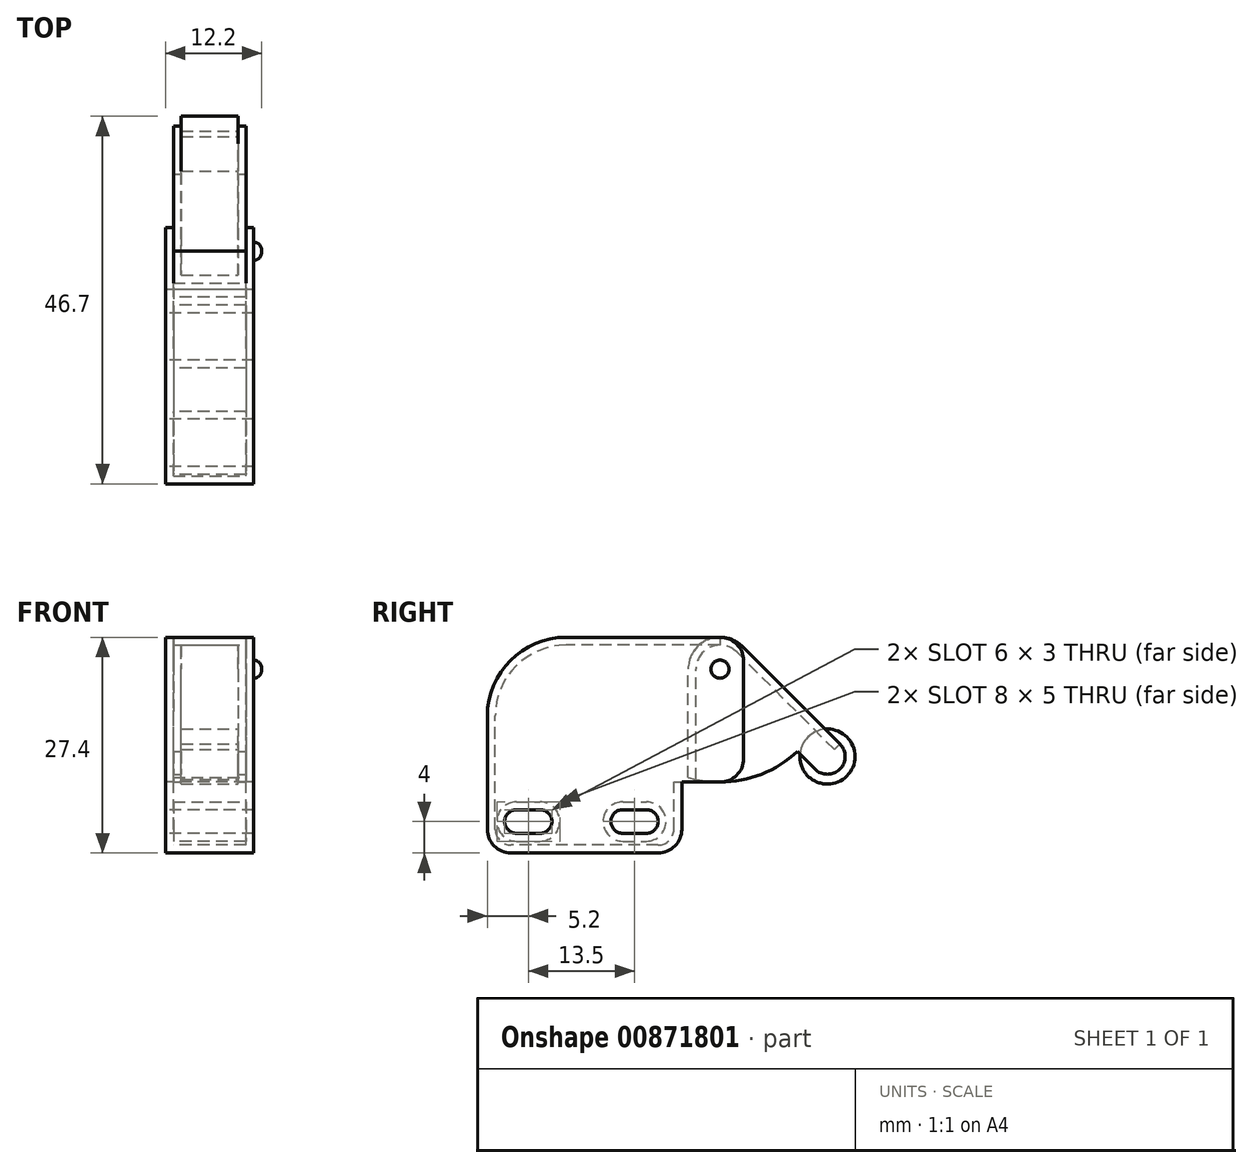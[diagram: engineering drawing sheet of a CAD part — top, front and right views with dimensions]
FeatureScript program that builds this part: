
annotation { "Feature Type Name" : "Feature", "Feature Type Description" : "" }
export const myFeature = defineFeature(function(context is Context, id is Id, definition is map)
    precondition{}
    {
        {
            var Q0;
            Q0=qCreatedBy(makeId("Right.planeOp"),FACE);
            var sketch = newSketch(context, id + "F0", { "sketchPlane" : qUnion([Q0])});
            skLineSegment(sketch, "E0.bottom", {"start": v(12.35, -13.7) * mm, "end": v(-12.35, -13.7) * mm});
            skLineSegment(sketch, "E0.top", {"start": v(12.35, 13.7) * mm, "end": v(-12.35, 13.7) * mm});
            skLineSegment(sketch, "E0.left", {"start": v(12.35, -13.7) * mm, "end": v(12.35, -4.7) * mm});
            skLineSegment(sketch, "E0.right", {"start": v(-12.35, -13.7) * mm, "end": v(-12.35, 13.7) * mm});
            skPoint(sketch, "E0.middle", {"position": v(0, 0) * mm});
            skLineSegment(sketch, "E1", {"start": v(-8.65, -9.7) * mm, "end": v(-5.65, -9.7) * mm});
            skLineSegment(sketch, "E2", {"start": v(4.85, -9.7) * mm, "end": v(7.85, -9.7) * mm});
            skPoint(sketch, "E3", {"position": v(-7.15, -9.7) * mm});
            skPoint(sketch, "E4", {"position": v(6.35, -9.7) * mm});
            skArc(sketch, "E5.0.startCap", {"start": v(-8.65, -11.2) * mm, "mid": v(-10.15, -9.7) * mm, "end": v(-8.65, -8.2) * mm});
            skArc(sketch, "E5.0.endCap", {"start": v(-5.65, -8.2) * mm, "mid": v(-4.15, -9.7) * mm, "end": v(-5.65, -11.2) * mm});
            skLineSegment(sketch, "E5.0.left", {"start": v(-8.65, -8.2) * mm, "end": v(-5.65, -8.2) * mm});
            skLineSegment(sketch, "E5.0.right", {"start": v(-8.65, -11.2) * mm, "end": v(-5.65, -11.2) * mm});
            skArc(sketch, "E5.1.startCap", {"start": v(7.85, -8.2) * mm, "mid": v(9.35, -9.7) * mm, "end": v(7.85, -11.2) * mm});
            skArc(sketch, "E5.1.endCap", {"start": v(4.85, -11.2) * mm, "mid": v(3.35, -9.7) * mm, "end": v(4.85, -8.2) * mm});
            skLineSegment(sketch, "E5.1.left", {"start": v(4.85, -11.2) * mm, "end": v(7.85, -11.2) * mm});
            skLineSegment(sketch, "E5.1.right", {"start": v(4.85, -8.2) * mm, "end": v(7.85, -8.2) * mm});
            skLineSegment(sketch, "E6", {"start": v(12.35, -4.7) * mm, "end": v(20.2, -4.7) * mm});
            skLineSegment(sketch, "E7", {"start": v(20.2, -4.7) * mm, "end": v(20.2, 13.7) * mm});
            skLineSegment(sketch, "E8", {"start": v(20.2, 13.7) * mm, "end": v(12.35, 13.7) * mm});
            skSolve(sketch);
        }
        {
            var Q0;
            Q0=makeQuery(id+"F0.imprint","IMPRINT",FACE,{"disambiguationData":[TD([[makeQuery(id+"F0.imprint","IMPRINT",EDGE,{"derivedFrom":sQuery(id+"F0.wireOp",EDGE,"E0.bottom")}),-1.0]])]});
            extrude(context, id + "F1", {"entities" : qUnion([Q0]), "depth" : 11.2 * mm, "offsetDistance" : 25 * mm});
        }
        {
            var Q0;
            Q0=makeQuery(id+"F1.opExtrude","SWEPT_EDGE",EDGE,{"disambiguationData":[OSD([sQuery(id+"F0.wireOp",EDGE,"E0.bottom"),sQuery(id+"F0.wireOp",EDGE,"E0.right")])]});
            var Q1;
            Q1=makeQuery(id+"F1.opExtrude","SWEPT_EDGE",EDGE,{"disambiguationData":[OSD([sQuery(id+"F0.wireOp",EDGE,"E0.bottom"),sQuery(id+"F0.wireOp",EDGE,"E0.left")])]});
            var Q2;
            Q2=makeQuery(id+"F1.opExtrude","SWEPT_EDGE",EDGE,{"disambiguationData":[OSD([sQuery(id+"F0.wireOp",EDGE,"E6"),sQuery(id+"F0.wireOp",EDGE,"E7")])]});
            var Q3;
            Q3=makeQuery(id+"F1.opExtrude","SWEPT_EDGE",EDGE,{"disambiguationData":[OSD([sQuery(id+"F0.wireOp",EDGE,"E7"),sQuery(id+"F0.wireOp",EDGE,"E8")])]});
            fillet(context, id + "F2", {"entities" : qUnion([Q0, Q1, Q2, Q3]), "tangentPropagation" : true, "radius" : 3 * mm, "defaultsChanged" : false, "vertexSettings" : [], "allowEdgeOverflow" : false});
        }
        {
            var Q0;
            Q0=makeQuery(id+"F1.opExtrude","SWEPT_EDGE",EDGE,{"disambiguationData":[OSD([sQuery(id+"F0.wireOp",EDGE,"E0.top"),sQuery(id+"F0.wireOp",EDGE,"E0.right")])]});
            fillet(context, id + "F3", {"entities" : qUnion([Q0]), "tangentPropagation" : true, "radius" : 10 * mm, "defaultsChanged" : true, "vertexSettings" : [], "allowEdgeOverflow" : false});
        }
        {
            var Q0;
            Q0=makeQuery(id+"F1.opExtrude","SWEPT_FACE",FACE,{"disambiguationData":[OSD([sQuery(id+"F0.wireOp",EDGE,"E6")])]});
            var Q1;
            Q1=makeQuery(id+"F2.opFillet","BLEND_FACE",FACE,{"disambiguationData":[OSD([sQuery(id+"F0.wireOp",EDGE,"E6"),sQuery(id+"F0.wireOp",EDGE,"E7")])]});
            var Q2;
            Q2=makeQuery(id+"F1.opExtrude","SWEPT_FACE",FACE,{"disambiguationData":[OSD([sQuery(id+"F0.wireOp",EDGE,"E7")])]});
            var Q3;
            Q3=makeQuery(id+"F2.opFillet","BLEND_FACE",FACE,{"disambiguationData":[OSD([sQuery(id+"F0.wireOp",EDGE,"E7"),sQuery(id+"F0.wireOp",EDGE,"E8")])]});
            shell(context, id + "F4", {"entities" : qUnion([Q0, Q1, Q2, Q3]), "thickness" : 1 * mm});
        }
        {
            var Q0;
            Q0=makeQuery(id+"F1.opExtrude","CAP_FACE",FACE,{"disambiguationData":[OSD([sQuery(id+"F0.wireOp",EDGE,"E0.bottom"),sQuery(id+"F0.wireOp",EDGE,"E0.top"),sQuery(id+"F0.wireOp",EDGE,"E0.left"),sQuery(id+"F0.wireOp",EDGE,"E0.right"),sQuery(id+"F0.wireOp",EDGE,"E5.0.startCap"),sQuery(id+"F0.wireOp",EDGE,"E5.0.endCap"),sQuery(id+"F0.wireOp",EDGE,"E5.0.left"),sQuery(id+"F0.wireOp",EDGE,"E5.0.right"),sQuery(id+"F0.wireOp",EDGE,"E5.1.startCap"),sQuery(id+"F0.wireOp",EDGE,"E5.1.endCap"),sQuery(id+"F0.wireOp",EDGE,"E5.1.left"),sQuery(id+"F0.wireOp",EDGE,"E5.1.right"),sQuery(id+"F0.wireOp",EDGE,"E6"),sQuery(id+"F0.wireOp",EDGE,"E7"),sQuery(id+"F0.wireOp",EDGE,"E8")])],"isStart":false});
            var sketch = newSketch(context, id + "F5", { "sketchPlane" : qUnion([Q0])});
            skCircle(sketch, "E9", {"center": v(17.2, 9.65) * mm, "radius": 1.15 * mm});
            skSolve(sketch);
        }
        {
            var Q0;
            Q0=makeQuery(id+"F5.imprint","IMPRINT",FACE,{"disambiguationData":[TD([[makeQuery(id+"F5.imprint","IMPRINT",EDGE,{"derivedFrom":sQuery(id+"F5.wireOp",EDGE,"E9")}),1.0]])]});
            extrude(context, id + "F6", {"entities" : qUnion([Q0]), "operationType" : NewBodyOperationType.ADD, "depth" : 1 * mm, "offsetDistance" : 25 * mm});
        }
        {
            var Q0;
            {var subQ0=sQuery(id+"F0.wireOp",EDGE,"E8");var subQ1=sQuery(id+"F0.wireOp",EDGE,"E7");var subQ2=sQuery(id+"F0.wireOp",EDGE,"E6");var subQ3=sQuery(id+"F0.wireOp",EDGE,"E5.1.right");var subQ4=sQuery(id+"F0.wireOp",EDGE,"E5.1.left");var subQ5=sQuery(id+"F0.wireOp",EDGE,"E5.1.endCap");var subQ6=sQuery(id+"F0.wireOp",EDGE,"E5.1.startCap");var subQ7=sQuery(id+"F0.wireOp",EDGE,"E5.0.right");var subQ8=sQuery(id+"F0.wireOp",EDGE,"E5.0.left");var subQ9=sQuery(id+"F0.wireOp",EDGE,"E5.0.endCap");var subQ10=sQuery(id+"F0.wireOp",EDGE,"E5.0.startCap");var subQ11=sQuery(id+"F0.wireOp",EDGE,"E0.right");var subQ12=sQuery(id+"F0.wireOp",EDGE,"E0.left");var subQ13=sQuery(id+"F0.wireOp",EDGE,"E0.top");var subQ14=sQuery(id+"F0.wireOp",EDGE,"E0.bottom");Q0=makeQuery(id+"F4.opShell","OFFSET_FACE",FACE,{"disambiguationData":[OSD([subQ14,subQ13,subQ12,subQ11,subQ10,subQ9,subQ8,subQ7,subQ6,subQ5,subQ4,subQ3,subQ2,subQ1,subQ0]),TDD([makeQuery(id+"F1.opExtrude","CAP_FACE",FACE,{"disambiguationData":[OSD([subQ14,subQ13,subQ12,subQ11,subQ10,subQ9,subQ8,subQ7,subQ6,subQ5,subQ4,subQ3,subQ2,subQ1,subQ0])],"isStart":false})])]});}
            var sketch = newSketch(context, id + "F7", { "sketchPlane" : qUnion([Q0])});
            skArc(sketch, "E10", {"start": v(-13.15, 9.65) * mm, "mid": v(-15.65, 13.4) * mm, "end": v(-20.06, 12.51) * mm});
            skLineSegment(sketch, "E11", {"start": v(-20.06, 12.51) * mm, "end": v(-32.44, 0.14) * mm});
            skArc(sketch, "E12", {"start": v(-32.44, 0.14) * mm, "mid": v(-32.44, -3.04) * mm, "end": v(-29.26, -3.04) * mm});
            skLineSegment(sketch, "E13", {"start": v(-29.26, -3.04) * mm, "end": v(-27.02, -0.81) * mm});
            skArc(sketch, "E14", {"start": v(-27.02, -0.81) * mm, "mid": v(-20.53, -4.3) * mm, "end": v(-13.15, -4.12) * mm});
            skLineSegment(sketch, "E15", {"start": v(-13.15, 9.65) * mm, "end": v(-13.15, -4.12) * mm});
            skSolve(sketch);
        }
        {
            var Q0;
            Q0 = qSketchRegion(id + "F7", true);
            var Q1;
            {var subQ0=sQuery(id+"F0.wireOp",EDGE,"E8");var subQ1=sQuery(id+"F0.wireOp",EDGE,"E7");var subQ2=sQuery(id+"F0.wireOp",EDGE,"E6");var subQ3=sQuery(id+"F0.wireOp",EDGE,"E5.1.right");var subQ4=sQuery(id+"F0.wireOp",EDGE,"E5.1.left");var subQ5=sQuery(id+"F0.wireOp",EDGE,"E5.1.endCap");var subQ6=sQuery(id+"F0.wireOp",EDGE,"E5.1.startCap");var subQ7=sQuery(id+"F0.wireOp",EDGE,"E5.0.right");var subQ8=sQuery(id+"F0.wireOp",EDGE,"E5.0.left");var subQ9=sQuery(id+"F0.wireOp",EDGE,"E5.0.endCap");var subQ10=sQuery(id+"F0.wireOp",EDGE,"E5.0.startCap");var subQ11=sQuery(id+"F0.wireOp",EDGE,"E0.right");var subQ12=sQuery(id+"F0.wireOp",EDGE,"E0.left");var subQ13=sQuery(id+"F0.wireOp",EDGE,"E0.top");var subQ14=sQuery(id+"F0.wireOp",EDGE,"E0.bottom");Q1=makeQuery(id+"F4.opShell","OFFSET_FACE",FACE,{"disambiguationData":[OSD([subQ14,subQ13,subQ12,subQ11,subQ10,subQ9,subQ8,subQ7,subQ6,subQ5,subQ4,subQ3,subQ2,subQ1,subQ0]),TDD([makeQuery(id+"F1.opExtrude","CAP_FACE",FACE,{"disambiguationData":[OSD([subQ14,subQ13,subQ12,subQ11,subQ10,subQ9,subQ8,subQ7,subQ6,subQ5,subQ4,subQ3,subQ2,subQ1,subQ0])],"isStart":true})])]});}
            extrude(context, id + "F8", {"entities" : qUnion([Q0]), "endBound" : BoundingType.UP_TO_SURFACE, "depth" : 25 * mm, "endBoundEntityFace" : qUnion([Q1]), "offsetDistance" : 25 * mm});
        }
        {
            var Q0;
            Q0=makeQuery(id+"F8.opExtrude","SWEPT_FACE",FACE,{"disambiguationData":[OSD([sQuery(id+"F7.wireOp",EDGE,"E14")])]});
            var Q1;
            Q1=makeQuery(id+"F8.opExtrude","SWEPT_FACE",FACE,{"disambiguationData":[OSD([sQuery(id+"F7.wireOp",EDGE,"E13")])]});
            var Q2;
            Q2=makeQuery(id+"F8.opExtrude","SWEPT_FACE",FACE,{"disambiguationData":[OSD([sQuery(id+"F7.wireOp",EDGE,"E12")])]});
            shell(context, id + "F9", {"entities" : qUnion([Q0, Q1, Q2]), "thickness" : 1 * mm});
        }
        {
            var Q0;
            {var subQ0=sQuery(id+"F7.wireOp",EDGE,"E15");var subQ1=sQuery(id+"F7.wireOp",EDGE,"E14");var subQ2=sQuery(id+"F7.wireOp",EDGE,"E13");var subQ3=sQuery(id+"F7.wireOp",EDGE,"E12");var subQ4=sQuery(id+"F7.wireOp",EDGE,"E11");var subQ5=sQuery(id+"F7.wireOp",EDGE,"E10");Q0=makeQuery(id+"F9.opShell","OFFSET_FACE",FACE,{"disambiguationData":[OSD([subQ5,subQ4,subQ3,subQ2,subQ1,subQ0]),TDD([makeQuery(id+"F8.opExtrude","CAP_FACE",FACE,{"disambiguationData":[OSD([subQ5,subQ4,subQ3,subQ2,subQ1,subQ0])],"isStart":true})])]});}
            var sketch = newSketch(context, id + "F10", { "sketchPlane" : qUnion([Q0])});
            skCircle(sketch, "E16", {"center": v(-30.85, -1.45) * mm, "radius": 3.5 * mm});
            skSolve(sketch);
        }
        {
            var Q0;
            Q0 = qSketchRegion(id + "F10", true);
            var Q1;
            {var subQ0=sQuery(id+"F7.wireOp",EDGE,"E15");var subQ1=sQuery(id+"F7.wireOp",EDGE,"E14");var subQ2=sQuery(id+"F7.wireOp",EDGE,"E13");var subQ3=sQuery(id+"F7.wireOp",EDGE,"E12");var subQ4=sQuery(id+"F7.wireOp",EDGE,"E11");var subQ5=sQuery(id+"F7.wireOp",EDGE,"E10");Q1=makeQuery(id+"F9.opShell","OFFSET_FACE",FACE,{"disambiguationData":[OSD([subQ5,subQ4,subQ3,subQ2,subQ1,subQ0]),TDD([makeQuery(id+"F8.opExtrude","CAP_FACE",FACE,{"disambiguationData":[OSD([subQ5,subQ4,subQ3,subQ2,subQ1,subQ0])],"isStart":false})])]});}
            extrude(context, id + "F11", {"entities" : qUnion([Q0]), "endBound" : BoundingType.UP_TO_SURFACE, "depth" : 25 * mm, "endBoundEntityFace" : qUnion([Q1]), "offsetDistance" : 25 * mm});
        }
        {
            var Q0;
            Q0=makeQuery(id+"F1.opExtrude","CAP_FACE",FACE,{"disambiguationData":[OSD([sQuery(id+"F0.wireOp",EDGE,"E0.bottom"),sQuery(id+"F0.wireOp",EDGE,"E0.top"),sQuery(id+"F0.wireOp",EDGE,"E0.left"),sQuery(id+"F0.wireOp",EDGE,"E0.right"),sQuery(id+"F0.wireOp",EDGE,"E5.0.startCap"),sQuery(id+"F0.wireOp",EDGE,"E5.0.endCap"),sQuery(id+"F0.wireOp",EDGE,"E5.0.left"),sQuery(id+"F0.wireOp",EDGE,"E5.0.right"),sQuery(id+"F0.wireOp",EDGE,"E5.1.startCap"),sQuery(id+"F0.wireOp",EDGE,"E5.1.endCap"),sQuery(id+"F0.wireOp",EDGE,"E5.1.left"),sQuery(id+"F0.wireOp",EDGE,"E5.1.right"),sQuery(id+"F0.wireOp",EDGE,"E6"),sQuery(id+"F0.wireOp",EDGE,"E7"),sQuery(id+"F0.wireOp",EDGE,"E8")])],"isStart":false});
            var Q1;
            Q1=makeQuery(id+"F1.opExtrude","CAP_FACE",FACE,{"disambiguationData":[OSD([sQuery(id+"F0.wireOp",EDGE,"E0.bottom"),sQuery(id+"F0.wireOp",EDGE,"E0.top"),sQuery(id+"F0.wireOp",EDGE,"E0.left"),sQuery(id+"F0.wireOp",EDGE,"E0.right"),sQuery(id+"F0.wireOp",EDGE,"E5.0.startCap"),sQuery(id+"F0.wireOp",EDGE,"E5.0.endCap"),sQuery(id+"F0.wireOp",EDGE,"E5.0.left"),sQuery(id+"F0.wireOp",EDGE,"E5.0.right"),sQuery(id+"F0.wireOp",EDGE,"E5.1.startCap"),sQuery(id+"F0.wireOp",EDGE,"E5.1.endCap"),sQuery(id+"F0.wireOp",EDGE,"E5.1.left"),sQuery(id+"F0.wireOp",EDGE,"E5.1.right"),sQuery(id+"F0.wireOp",EDGE,"E6"),sQuery(id+"F0.wireOp",EDGE,"E7"),sQuery(id+"F0.wireOp",EDGE,"E8")])],"isStart":true});
            cPlane(context, id + "F12", {"entities" : qUnion([Q0, Q1]), "cplaneType" : CPlaneType.MID_PLANE, "offset" : 25 * mm, "width" : 150 * mm, "height" : 150 * mm});
        }
        {
            var Q0;
            Q0=makeQuery(id+"F6.opExtrude","CAP_EDGE",EDGE,{"disambiguationData":[OSD([sQuery(id+"F5.wireOp",EDGE,"E9")])],"isStart":false});
            var Q1;
            Q1=makeQuery(id+"Fypl3w4P4VfX40Y_3.1.F6.opExtrude","CAP_EDGE",EDGE,{"disambiguationData":[OSD([sQuery(id+"F5.wireOp",EDGE,"E9")])],"isStart":false});
            fillet(context, id + "F13", {"entities" : qUnion([Q0, Q1]), "tangentPropagation" : true, "radius" : 1 * mm, "defaultsChanged" : false, "vertexSettings" : [], "allowEdgeOverflow" : false});
        }
    });
